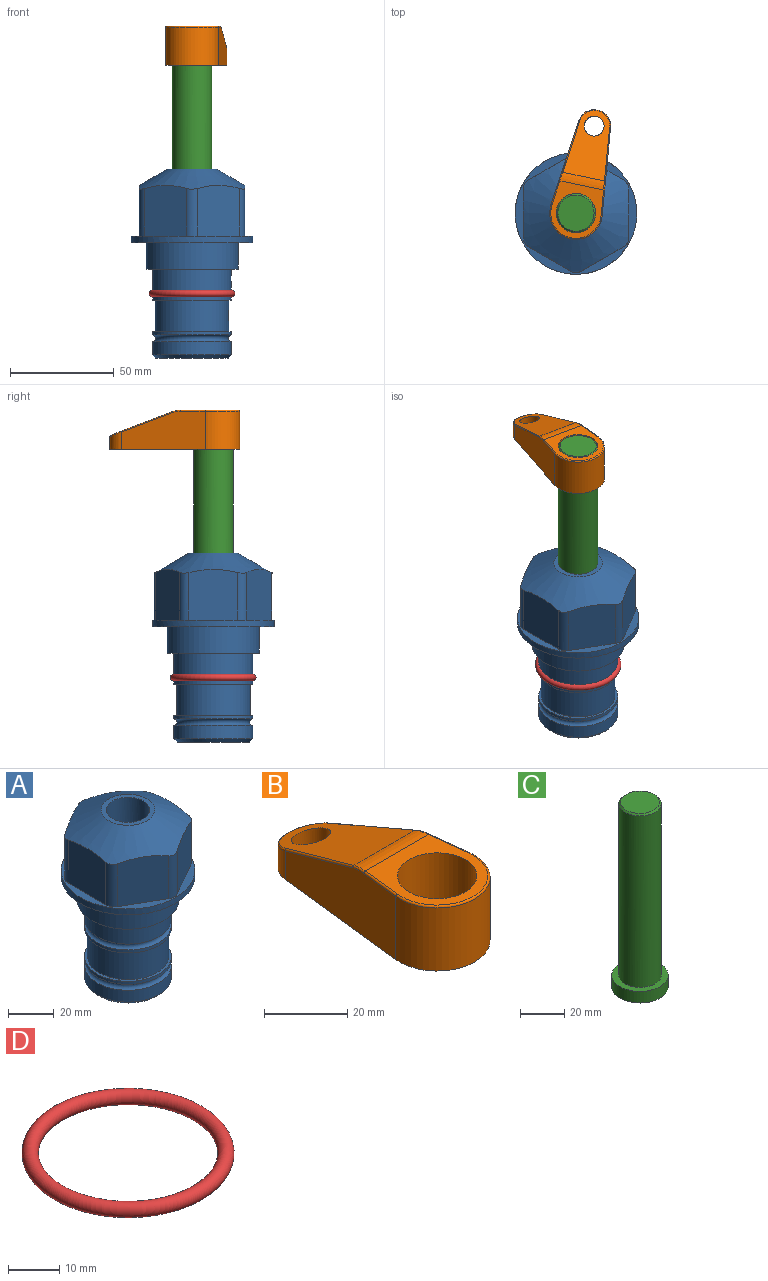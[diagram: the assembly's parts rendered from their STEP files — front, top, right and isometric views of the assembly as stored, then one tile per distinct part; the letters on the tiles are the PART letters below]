
ASSEMBLY  parts=4 mates=2
PART A: 36 faces, bbox 58.7x58.7x91.2 mm
  f0: cylinder r=17.78mm len=35.56mm, axis (0,0,1), area 1670.8mm2, adj f23,f24,f31
  f1: cylinder r=19.05mm len=38.1mm, axis (0,0,1), area 1191.9mm2, adj f26,f27,f30
  f2: plane 58.66x58.66mm, normal (0,0,-1), area 1150.6mm2, adj f3,f28
  f3: cylinder r=29.33mm len=58.66mm, axis (0,0,-1), area 585.1mm2, adj f2,f4
  f4: plane 58.66x58.66mm, normal (0,0,1), area 475.9mm2, adj f3,f5,f6,f7,f8,f9,f10,f11
  f5: plane 24.5x20.32mm, normal (-0.5,0.87,0), area 562.8mm2, adj f4,f15,f16,f17
  f6: plane 24.5x20.32mm, normal (0.5,0.87,0), area 562.8mm2, adj f4,f14,f15,f17
  f7: plane 24.5x23.48mm, normal (1,0,0), area 562.8mm2, adj f4,f13,f14,f17
  f8: plane 24.5x20.32mm, normal (0.5,-0.87,0), area 562.8mm2, adj f4,f12,f13,f17
  f9: plane 24.5x20.32mm, normal (-0.5,-0.87,0), area 562.8mm2, adj f4,f11,f12,f17
  f10: plane 24.5x23.48mm, normal (-1,0,0), area 562.8mm2, adj f4,f11,f16,f17
  f11: cylinder r=5.08mm len=23.01mm, axis (0,0,-1), area 121.2mm2, adj f4,f9,f10,f17
  f12: cylinder r=5.08mm len=23.01mm, axis (0,0,-1), area 121.2mm2, adj f4,f8,f9,f17
  f13: cylinder r=5.08mm len=23.01mm, axis (0,0,-1), area 121.2mm2, adj f4,f7,f8,f17
  f14: cylinder r=5.08mm len=23.01mm, axis (0,0,-1), area 121.2mm2, adj f4,f6,f7,f17
  f15: cylinder r=5.08mm len=23.01mm, axis (0,0,-1), area 121.2mm2, adj f4,f5,f6,f17
  f16: cylinder r=5.08mm len=23.01mm, axis (0,0,-1), area 121.2mm2, adj f4,f5,f10,f17
  f17: cone r=11.73mm half-angle=60deg, axis (0,0,-1), area 2071.8mm2, adj f5,f6,f7,f8,f9,f10,f11,f12
  f18: plane 23.46x23.46mm, normal (0,0,1), area 147.4mm2, adj f17,f35
  f19: plane 34.93x34.93mm, normal (0,0,-1), area 958mm2, adj f29
  f20: cylinder r=19.05mm len=38.1mm, axis (0,0,1), area 760.1mm2, adj f21,f29
  f21: torus R=19.05mm, axis (0,0,1), area 565.3mm2, adj f20,f22
  f22: cylinder r=19.05mm len=38.1mm, axis (0,0,1), area 190mm2, adj f21,f23
  f23: plane 38.1x38.1mm, normal (0,0,1), area 146.9mm2, adj f0,f22
  f24: plane 38.1x38.1mm, normal (0,0,-1), area 146.9mm2, adj f0,f25
  f25: cylinder r=19.05mm len=38.1mm, axis (0,0,1), area 190mm2, adj f24,f26
  f26: torus R=19.05mm, axis (0,0,1), area 565.3mm2, adj f1,f25
  f27: plane 44.45x44.45mm, normal (0,0,-1), area 411.7mm2, adj f1,f28
  f28: cylinder r=22.23mm len=44.45mm, axis (0,0,1), area 1773.5mm2, adj f2,f27
  f29: cone r=19.05mm half-angle=45deg, axis (0,0,1), area 257.5mm2, adj f19,f20
  f30: cylinder r=3.17mm len=6.75mm, axis (-1,0,0), area 128mm2, adj f1,f33
  f31: cylinder r=3.17mm len=6.35mm, axis (-1,0,0), area 102.5mm2, adj f0,f33
  f32: plane 25.4x25.4mm, normal (0,0,1), area 506.7mm2, adj f33
  f33: cylinder r=12.7mm len=66.42mm, axis (0,0,-1), area 5236.2mm2, adj f30,f31,f32,f34
  f34: cone r=9.53mm half-angle=30deg, axis (0,0,-1), area 443.4mm2, adj f33,f35
  f35: cylinder r=9.53mm len=19.05mm, axis (0,0,-1), area 849mm2, adj f18,f34
PART B: 44 faces, bbox 27.5x64.5x19.1 mm
  f0: plane 2.3x0.95mm, normal (0,0,-1), area 1mm2, adj f25,f30,f34
  f1: plane 63.5x25.4mm, normal (0,0,-1), area 561.7mm2, adj f2,f3,f4,f5,f6,f7,f19,f20
  f2: cylinder r=12.7mm len=25.4mm, axis (0,0,-1), area 792.2mm2, adj f1,f3,f5,f13
  f3: plane 42.33x18.54mm, normal (0.99,0.11,0), area 647mm2, adj f1,f2,f4,f11,f12,f14
  f4: cylinder r=7.94mm len=15.78mm, axis (0,0,-1), area 158.6mm2, adj f1,f3,f5,f16
  f5: plane 42.33x18.54mm, normal (-0.99,0.11,0), area 647mm2, adj f1,f2,f4,f15,f17,f18
  f6: cylinder r=9.53mm len=19.05mm, axis (0,0,-1), area 1140.1mm2, adj f1,f8
  f7: cylinder r=4.76mm len=10.98mm, axis (0,0,-1), area 276.1mm2, adj f1,f9
  f8: plane 25.83x24.38mm, normal (0,0,1), area 262.2mm2, adj f6,f10,f11,f13,f15
  f9: plane 32.49x20.55mm, normal (0,0.34,0.94), area 489.9mm2, adj f7,f10,f14,f16,f18
  f10: cylinder r=12.7mm len=21.49mm, axis (-1,0,0), area 93.2mm2, adj f8,f9,f12,f17
  f11: cylinder r=0.51mm len=12.34mm, axis (0.11,-0.99,0), area 9.9mm2, adj f3,f8,f12,f13
  f12: bspline ~7.62x1.64mm, area 3.5mm2, adj f3,f10,f11,f14
  f13: torus R=12.19mm, axis (0,0,1), area 33.6mm2, adj f2,f8,f11,f15
  f14: cylinder r=0.51mm len=26.01mm, axis (0.1,-0.93,0.34), area 21.6mm2, adj f3,f9,f12,f16
  f15: cylinder r=0.51mm len=12.34mm, axis (0.11,0.99,0), area 9.9mm2, adj f5,f8,f13,f17
  f16: bspline ~15.78x7.05mm, area 15.7mm2, adj f4,f9,f14,f18
  f17: bspline ~7.62x1.64mm, area 3.5mm2, adj f5,f10,f15,f18
  f18: cylinder r=0.51mm len=26.01mm, axis (0.1,0.93,-0.34), area 21.6mm2, adj f5,f9,f16,f17
  f19: plane 21.6x14.29mm, normal (-0.99,-0.11,0), area 242.6mm2, adj f1,f26,f28,f34,f36,f38
  f20: plane 21.6x14.29mm, normal (0.99,-0.11,0), area 242.6mm2, adj f1,f27,f29,f37,f39,f41
  f21: cylinder r=12.7mm len=14.29mm, axis (0,0,-1), area 173.2mm2, adj f1,f26,f27,f30,f31,f33
  f22: cylinder r=7.94mm len=7.63mm, axis (0,0,-1), area 53.8mm2, adj f1,f28,f29,f42
  f23: plane 2.3x0.95mm, normal (0,0,-1), area 1mm2, adj f25,f33,f37
  f24: plane 17.94x12.32mm, normal (0,-0.34,-0.94), area 191.2mm2, adj f25,f38,f41,f42
  f25: cylinder r=9.53mm len=12.93mm, axis (-1,0,0), area 37.5mm2, adj f0,f23,f24,f31,f36,f39
  f26: cylinder r=1.59mm len=14.29mm, axis (0,0,-1), area 49mm2, adj f1,f19,f21,f32
  f27: cylinder r=1.59mm len=14.29mm, axis (0,0,-1), area 49mm2, adj f1,f20,f21,f35
  f28: cylinder r=1.59mm len=7.28mm, axis (0,0,-1), area 22.1mm2, adj f1,f19,f22,f40
  f29: cylinder r=1.59mm len=7.28mm, axis (0,0,-1), area 22.1mm2, adj f1,f20,f22,f43
  f30: torus R=14.29mm, axis (0,0,1), area 5.8mm2, adj f0,f21,f31,f32
  f31: bspline ~11.06x2.73mm, area 20.8mm2, adj f21,f25,f30,f33
  f32: sphere r=1.59mm, area 5.4mm2, adj f26,f30,f34
  f33: torus R=14.29mm, axis (0,0,1), area 5.8mm2, adj f21,f23,f31,f35
  f34: cylinder r=1.59mm len=1.68mm, axis (-0.11,0.99,0), area 2.4mm2, adj f0,f19,f32,f36
  f35: sphere r=1.59mm, area 5.4mm2, adj f27,f33,f37
  f36: bspline ~5.82x2.33mm, area 7.7mm2, adj f19,f25,f34,f38
  f37: cylinder r=1.59mm len=1.68mm, axis (0.11,0.99,0), area 2.4mm2, adj f20,f23,f35,f39
  f38: cylinder r=1.59mm len=18.33mm, axis (0.1,-0.93,0.34), area 46.7mm2, adj f19,f24,f36,f40
  f39: bspline ~5.82x2.33mm, area 7.7mm2, adj f20,f25,f37,f41
  f40: sphere r=1.59mm, area 3.6mm2, adj f28,f38,f42
  f41: cylinder r=1.59mm len=18.33mm, axis (0.1,0.93,-0.34), area 46.7mm2, adj f20,f24,f39,f43
  f42: bspline ~8.31x1.84mm, area 15.3mm2, adj f22,f24,f40,f43
  f43: sphere r=1.59mm, area 3.6mm2, adj f29,f41,f42
PART C: 6 faces, bbox 25.4x25.4x101.6 mm
  f0: plane 17.46x17.46mm, normal (0,0,1), area 239.5mm2, adj f5
  f1: plane 25.4x25.4mm, normal (0,0,-1), area 506.7mm2, adj f2
  f2: cylinder r=12.7mm len=25.4mm, axis (0,0,1), area 506.7mm2, adj f1,f3
  f3: plane 25.4x25.4mm, normal (0,0,1), area 221.7mm2, adj f2,f4
  f4: cylinder r=9.53mm len=94.46mm, axis (0,0,1), area 5653mm2, adj f3,f5
  f5: cone r=8.73mm half-angle=45deg, axis (0,0,-1), area 64.4mm2, adj f0,f4
PART D: 1 faces, bbox 44.7x44.7x3.2 mm
  f0: torus R=19.05mm, axis (0,0,1), area 1193.9mm2
PLACE A at identity fixed
PLACE B rot(axis=(0,0,-1),11.8deg) t=(0,0,85.52)mm
PLACE C rot(axis=(0,0,-1),11.8deg) t=(0,0,30.91)mm
PLACE D at identity
MATE cylindrical C.f2 <-> A.f0  axis (0,0,1) through (0,0,56.55)mm
MATE fastened B.f2 <-> C.f2  axis (0,0,-1) through (0,0,104.57)mm
